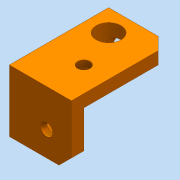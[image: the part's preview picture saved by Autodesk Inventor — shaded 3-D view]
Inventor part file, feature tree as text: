
AUTODESK INVENTOR PART (.ipt)
format: ipt  version: 2016 (Build 200138000, 138)  size: 140,288 bytes
history: native  units: mm (DEFAULTED — no unit token found)
features: sketch x5, other x3
ambient origin geometry x8: Origin, YZ Plane, XZ Plane, XY Plane, X Axis, Y Axis, Z Axis, Center Point
bodies: Solid1 (feature_tree)
feature tree (8):
  other  "Frame3WayBlockMotor.ipt"
  other  "Solid1::Frame3WayBlockMotor.ipt"
  other  "TaggingFeature1"
  sketch  "Sketch1"  dims[d0=10.0mm]
  sketch  "Sketch2"
  sketch  "Sketch3"
  sketch  "Sketch4"
  sketch  "Sketch5"
